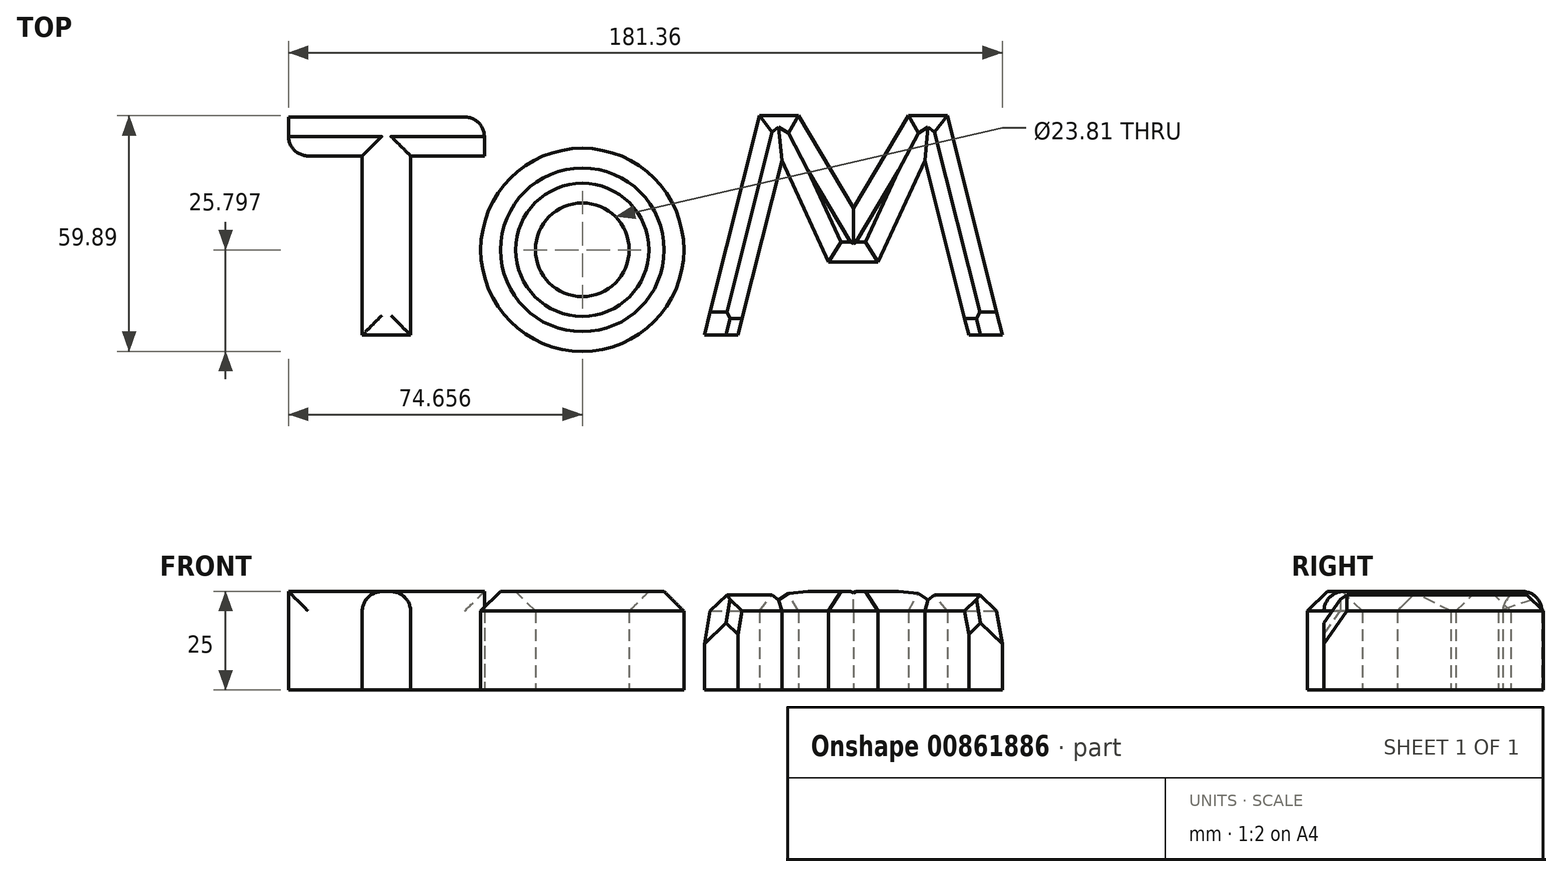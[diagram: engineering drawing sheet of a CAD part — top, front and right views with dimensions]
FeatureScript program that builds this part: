
annotation { "Feature Type Name" : "Feature", "Feature Type Description" : "" }
export const myFeature = defineFeature(function(context is Context, id is Id, definition is map)
    precondition{}
    {
        {
            var Q0;
            Q0=qCreatedBy(makeId("Top.planeOp"),FACE);
            var sketch = newSketch(context, id + "F0", { "sketchPlane" : qUnion([Q0])});
            skLineSegment(sketch, "E0", {"start": v(-49.77, 0) * mm, "end": v(-49.77, 45.51) * mm});
            skLineSegment(sketch, "E1", {"start": v(-49.77, 45.51) * mm, "end": v(-68.52, 45.51) * mm});
            skLineSegment(sketch, "E2", {"start": v(-68.52, 45.51) * mm, "end": v(-68.52, 55.4) * mm});
            skLineSegment(sketch, "E3", {"start": v(-68.52, 55.4) * mm, "end": v(-18.75, 55.4) * mm});
            skLineSegment(sketch, "E4", {"start": v(-18.75, 55.4) * mm, "end": v(-18.75, 45.51) * mm});
            skLineSegment(sketch, "E5", {"start": v(-18.75, 45.51) * mm, "end": v(-37.5, 45.51) * mm});
            skLineSegment(sketch, "E6", {"start": v(-37.5, 45.51) * mm, "end": v(-37.5, 0) * mm});
            skLineSegment(sketch, "E7", {"start": v(-37.5, 0) * mm, "end": v(-49.77, 0) * mm});
            skSolve(sketch);
        }
        {
            var Q0;
            Q0=qCreatedBy(makeId("Top.planeOp"),FACE);
            var sketch = newSketch(context, id + "F1", { "sketchPlane" : qUnion([Q0])});
            skCircle(sketch, "E8", {"center": v(6.14, 21.65) * mm, "radius": 25.8 * mm});
            skCircle(sketch, "E9", {"center": v(6.14, 21.65) * mm, "radius": 11.9 * mm});
            skSolve(sketch);
        }
        {
            var Q0;
            Q0=qCreatedBy(makeId("Top.planeOp"),FACE);
            var sketch = newSketch(context, id + "F2", { "sketchPlane" : qUnion([Q0])});
            skLineSegment(sketch, "E10", {"start": v(37.16, 0) * mm, "end": v(51.14, 55.74) * mm});
            skLineSegment(sketch, "E11", {"start": v(51.14, 55.74) * mm, "end": v(61.02, 55.74) * mm});
            skLineSegment(sketch, "E12", {"start": v(37.16, 0) * mm, "end": v(45.68, 0) * mm});
            skLineSegment(sketch, "E13", {"start": v(45.68, 0) * mm, "end": v(56.8, 44.35) * mm});
            skLineSegment(sketch, "E14", {"start": v(56.8, 44.35) * mm, "end": v(68.71, 18.6) * mm});
            skLineSegment(sketch, "E15", {"start": v(68.71, 18.6) * mm, "end": v(75, 18.6) * mm});
            skLineSegment(sketch, "E16", {"start": v(61.02, 55.74) * mm, "end": v(75, 32.22) * mm});
            skLineSegment(sketch, "E17", {"start": v(75, 32.22) * mm, "end": v(75, 18.6) * mm});
            skLineSegment(sketch, "E18.MirrorCS", {"start": v(81.29, 18.6) * mm, "end": v(75, 18.6) * mm});
            skLineSegment(sketch, "E19.MirrorCS", {"start": v(112.84, 0) * mm, "end": v(104.32, 0) * mm});
            skLineSegment(sketch, "E20.MirrorCS", {"start": v(88.98, 55.74) * mm, "end": v(75, 32.22) * mm});
            skLineSegment(sketch, "E21.MirrorCS", {"start": v(112.84, 0) * mm, "end": v(98.86, 55.74) * mm});
            skLineSegment(sketch, "E22.MirrorCS", {"start": v(104.32, 0) * mm, "end": v(93.2, 44.35) * mm});
            skLineSegment(sketch, "E23.MirrorCS", {"start": v(98.86, 55.74) * mm, "end": v(88.98, 55.74) * mm});
            skLineSegment(sketch, "E24.MirrorCS", {"start": v(93.2, 44.35) * mm, "end": v(81.29, 18.6) * mm});
            skSolve(sketch);
        }
        {
            var Q0;
            Q0=makeQuery(id+"F0.imprint","IMPRINT",FACE,{"disambiguationData":[TD([[makeQuery(id+"F0.imprint","IMPRINT",EDGE,{"derivedFrom":sQuery(id+"F0.wireOp",EDGE,"E0")}),-1.0]])]});
            var Q1;
            Q1=makeQuery(id+"F1.imprint","IMPRINT",FACE,{"disambiguationData":[TD([[makeQuery(id+"F1.imprint","IMPRINT",EDGE,{"derivedFrom":sQuery(id+"F1.wireOp",EDGE,"E8")}),1.0]])]});
            var Q2;
            Q2=makeQuery(id+"F2.imprint","IMPRINT",FACE,{"disambiguationData":[TD([[makeQuery(id+"F2.imprint","IMPRINT",EDGE,{"derivedFrom":sQuery(id+"F2.wireOp",EDGE,"E10")}),-1.0]])]});
            var Q3;
            Q3=makeQuery(id+"F2.imprint","IMPRINT",FACE,{"disambiguationData":[TD([[makeQuery(id+"F2.imprint","IMPRINT",EDGE,{"derivedFrom":sQuery(id+"F2.wireOp",EDGE,"E17")}),1.0]])]});
            extrude(context, id + "F3", {"entities" : qUnion([Q0, Q1, Q2, Q3]), "depth" : 25 * mm, "offsetDistance" : 25 * mm});
        }
        {
            var Q0;
            Q0=makeQuery(id+"F3.opExtrude","CAP_EDGE",EDGE,{"disambiguationData":[OSD([sQuery(id+"F0.wireOp",EDGE,"E0")])],"isStart":false});
            var Q1;
            Q1=makeQuery(id+"F3.opExtrude","CAP_EDGE",EDGE,{"disambiguationData":[OSD([sQuery(id+"F0.wireOp",EDGE,"E6")])],"isStart":false});
            var Q2;
            Q2=makeQuery(id+"F3.opExtrude","CAP_EDGE",EDGE,{"disambiguationData":[OSD([sQuery(id+"F0.wireOp",EDGE,"E1")])],"isStart":false});
            var Q3;
            Q3=makeQuery(id+"F3.opExtrude","CAP_EDGE",EDGE,{"disambiguationData":[OSD([sQuery(id+"F0.wireOp",EDGE,"E3")])],"isStart":false});
            var Q4;
            Q4=makeQuery(id+"F3.opExtrude","CAP_EDGE",EDGE,{"disambiguationData":[OSD([sQuery(id+"F0.wireOp",EDGE,"E5")])],"isStart":false});
            var Q5;
            Q5=makeQuery(id+"F3.opExtrude","CAP_EDGE",EDGE,{"disambiguationData":[OSD([sQuery(id+"F0.wireOp",EDGE,"E7")])],"isStart":false});
            fillet(context, id + "F4", {"entities" : qUnion([Q0, Q1, Q2, Q3, Q4, Q5]), "radius" : 5 * mm, "tangentPropagation" : true, "allowEdgeOverflow" : false});
        }
        {
            var Q0;
            Q0=makeQuery(id+"F4.opFillet","BLEND_EDGE",EDGE,{"blendedFrom":[makeQuery(id+"F3.opExtrude","CAP_EDGE",EDGE,{"disambiguationData":[OSD([sQuery(id+"F0.wireOp",EDGE,"E1")])],"isStart":false}),makeQuery(id+"F3.opExtrude","SWEPT_FACE",FACE,{"disambiguationData":[OSD([sQuery(id+"F0.wireOp",EDGE,"E2")])]})],"blendedInto":[makeQuery(id+"F3.opExtrude","SWEPT_FACE",FACE,{"disambiguationData":[OSD([sQuery(id+"F0.wireOp",EDGE,"E2")])]})]});
            var Q1;
            Q1=makeQuery(id+"F4.opFillet","BLEND_EDGE",EDGE,{"blendedFrom":[makeQuery(id+"F3.opExtrude","CAP_EDGE",EDGE,{"disambiguationData":[OSD([sQuery(id+"F0.wireOp",EDGE,"E3")])],"isStart":false}),makeQuery(id+"F3.opExtrude","SWEPT_FACE",FACE,{"disambiguationData":[OSD([sQuery(id+"F0.wireOp",EDGE,"E4")])]})],"blendedInto":[makeQuery(id+"F3.opExtrude","SWEPT_FACE",FACE,{"disambiguationData":[OSD([sQuery(id+"F0.wireOp",EDGE,"E4")])]})]});
            fillet(context, id + "F5", {"entities" : qUnion([Q0, Q1]), "radius" : 5 * mm, "tangentPropagation" : true, "allowEdgeOverflow" : false});
        }
        {
            var Q0;
            Q0=makeQuery(id+"F3.opExtrude","CAP_EDGE",EDGE,{"disambiguationData":[OSD([sQuery(id+"F1.wireOp",EDGE,"E8")])],"isStart":false});
            var Q1;
            Q1=makeQuery(id+"F3.opExtrude","CAP_EDGE",EDGE,{"disambiguationData":[OSD([sQuery(id+"F1.wireOp",EDGE,"E9")])],"isStart":false});
            chamfer(context, id + "F6", {"entities" : qUnion([Q0, Q1]), "width" : 5 * mm, "tangentPropagation" : true});
        }
        {
            var Q0;
            Q0=makeQuery(id+"F3.opExtrude","CAP_EDGE",EDGE,{"disambiguationData":[OSD([sQuery(id+"F2.wireOp",EDGE,"E10")])],"isStart":false});
            var Q1;
            Q1=makeQuery(id+"F3.opExtrude","CAP_EDGE",EDGE,{"disambiguationData":[OSD([sQuery(id+"F2.wireOp",EDGE,"E13")])],"isStart":false});
            var Q2;
            Q2=makeQuery(id+"F3.opExtrude","CAP_EDGE",EDGE,{"disambiguationData":[OSD([sQuery(id+"F2.wireOp",EDGE,"E11")])],"isStart":false});
            var Q3;
            Q3=makeQuery(id+"F3.opExtrude","CAP_EDGE",EDGE,{"disambiguationData":[OSD([sQuery(id+"F2.wireOp",EDGE,"E14")])],"isStart":false});
            var Q4;
            Q4=makeQuery(id+"F3.opExtrude","CAP_EDGE",EDGE,{"disambiguationData":[OSD([sQuery(id+"F2.wireOp",EDGE,"E16")])],"isStart":false});
            var Q5;
            Q5=makeQuery(id+"F3.opExtrude","CAP_EDGE",EDGE,{"disambiguationData":[OSD([sQuery(id+"F2.wireOp",EDGE,"E15"),sQuery(id+"F2.wireOp",EDGE,"E18.MirrorCS")])],"isStart":false});
            var Q6;
            Q6=makeQuery(id+"F3.opExtrude","CAP_EDGE",EDGE,{"disambiguationData":[OSD([sQuery(id+"F2.wireOp",EDGE,"E24.MirrorCS")])],"isStart":false});
            var Q7;
            Q7=makeQuery(id+"F3.opExtrude","CAP_EDGE",EDGE,{"disambiguationData":[OSD([sQuery(id+"F2.wireOp",EDGE,"E20.MirrorCS")])],"isStart":false});
            var Q8;
            Q8=makeQuery(id+"F3.opExtrude","CAP_EDGE",EDGE,{"disambiguationData":[OSD([sQuery(id+"F2.wireOp",EDGE,"E23.MirrorCS")])],"isStart":false});
            var Q9;
            Q9=makeQuery(id+"F3.opExtrude","CAP_EDGE",EDGE,{"disambiguationData":[OSD([sQuery(id+"F2.wireOp",EDGE,"E21.MirrorCS")])],"isStart":false});
            var Q10;
            Q10=makeQuery(id+"F3.opExtrude","CAP_EDGE",EDGE,{"disambiguationData":[OSD([sQuery(id+"F2.wireOp",EDGE,"E22.MirrorCS")])],"isStart":false});
            chamfer(context, id + "F7", {"entities" : qUnion([Q0, Q1, Q2, Q3, Q4, Q5, Q6, Q7, Q8, Q9, Q10]), "width" : 5 * mm, "tangentPropagation" : true});
        }
        {
            var Q0;
            Q0=makeQuery(id+"F7.opChamfer","BLEND_EDGE",EDGE,{"blendedFrom":[makeQuery(id+"F3.opExtrude","CAP_EDGE",EDGE,{"disambiguationData":[OSD([sQuery(id+"F2.wireOp",EDGE,"E10")])],"isStart":false}),makeQuery(id+"F3.opExtrude","SWEPT_FACE",FACE,{"disambiguationData":[OSD([sQuery(id+"F2.wireOp",EDGE,"E12")])]})],"blendedInto":[makeQuery(id+"F3.opExtrude","SWEPT_FACE",FACE,{"disambiguationData":[OSD([sQuery(id+"F2.wireOp",EDGE,"E12")])]})]});
            var Q1;
            Q1=makeQuery(id+"F7.opChamfer","BLEND_EDGE",EDGE,{"blendedFrom":[makeQuery(id+"F3.opExtrude","CAP_EDGE",EDGE,{"disambiguationData":[OSD([sQuery(id+"F2.wireOp",EDGE,"E13")])],"isStart":false}),makeQuery(id+"F3.opExtrude","SWEPT_FACE",FACE,{"disambiguationData":[OSD([sQuery(id+"F2.wireOp",EDGE,"E12")])]})],"blendedInto":[makeQuery(id+"F3.opExtrude","SWEPT_FACE",FACE,{"disambiguationData":[OSD([sQuery(id+"F2.wireOp",EDGE,"E12")])]})]});
            var Q2;
            Q2=makeQuery(id+"F7.opChamfer","BLEND_EDGE",EDGE,{"blendedFrom":[makeQuery(id+"F3.opExtrude","CAP_EDGE",EDGE,{"disambiguationData":[OSD([sQuery(id+"F2.wireOp",EDGE,"E22.MirrorCS")])],"isStart":false}),makeQuery(id+"F3.opExtrude","SWEPT_FACE",FACE,{"disambiguationData":[OSD([sQuery(id+"F2.wireOp",EDGE,"E19.MirrorCS")])]})],"blendedInto":[makeQuery(id+"F3.opExtrude","SWEPT_FACE",FACE,{"disambiguationData":[OSD([sQuery(id+"F2.wireOp",EDGE,"E19.MirrorCS")])]})]});
            var Q3;
            Q3=makeQuery(id+"F7.opChamfer","BLEND_EDGE",EDGE,{"blendedFrom":[makeQuery(id+"F3.opExtrude","CAP_EDGE",EDGE,{"disambiguationData":[OSD([sQuery(id+"F2.wireOp",EDGE,"E21.MirrorCS")])],"isStart":false}),makeQuery(id+"F3.opExtrude","SWEPT_FACE",FACE,{"disambiguationData":[OSD([sQuery(id+"F2.wireOp",EDGE,"E19.MirrorCS")])]})],"blendedInto":[makeQuery(id+"F3.opExtrude","SWEPT_FACE",FACE,{"disambiguationData":[OSD([sQuery(id+"F2.wireOp",EDGE,"E19.MirrorCS")])]})]});
            chamfer(context, id + "F8", {"entities" : qUnion([Q0, Q1, Q2, Q3]), "width" : 5 * mm, "tangentPropagation" : true});
        }
    });
